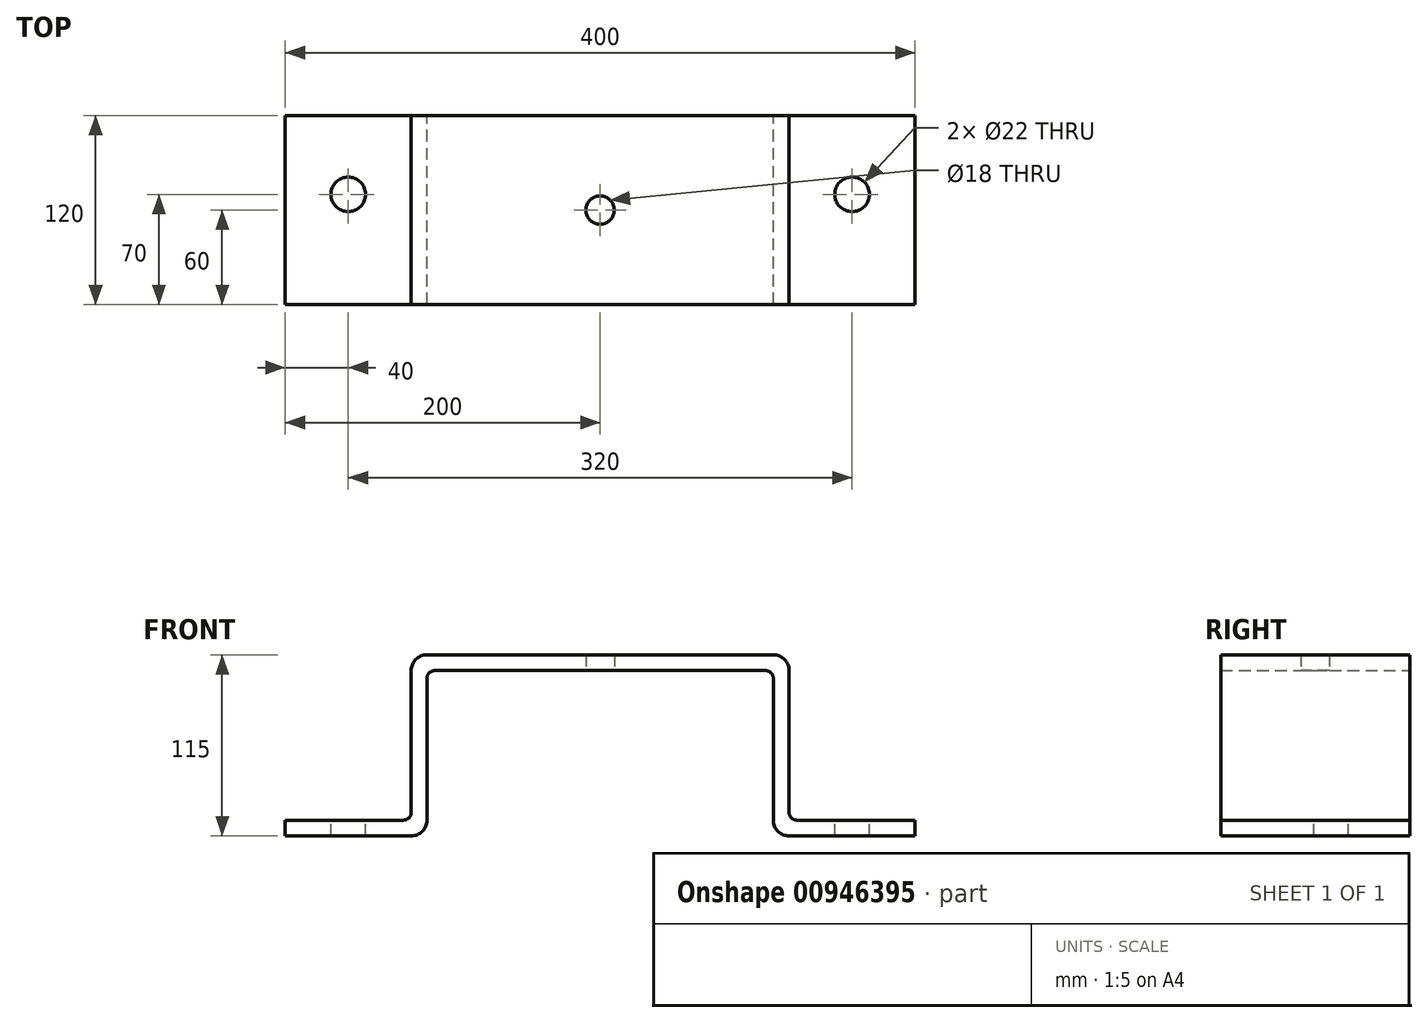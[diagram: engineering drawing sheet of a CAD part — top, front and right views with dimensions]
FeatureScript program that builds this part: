
annotation { "Feature Type Name" : "Feature", "Feature Type Description" : "" }
export const myFeature = defineFeature(function(context is Context, id is Id, definition is map)
    precondition{}
    {
        {
            var Q0;
            Q0=qCreatedBy(makeId("Front.planeOp"),FACE);
            var sketch = newSketch(context, id + "F0", { "sketchPlane" : qUnion([Q0])});
            skLineSegment(sketch, "E0.bottom", {"start": v(-200, 0) * mm, "end": v(200, 0) * mm});
            skLineSegment(sketch, "E0.top", {"start": v(-200, 115) * mm, "end": v(200, 115) * mm});
            skLineSegment(sketch, "E0.left", {"start": v(-200, 0) * mm, "end": v(-200, 115) * mm});
            skLineSegment(sketch, "E0.right", {"start": v(200, 0) * mm, "end": v(200, 115) * mm});
            skPoint(sketch, "E1", {"position": v(0, 0) * mm});
            skLineSegment(sketch, "E2", {"start": v(0, 0) * mm, "end": v(0, 115) * mm, "construction": true});
            skPoint(sketch, "E3", {"position": v(0, 52.5) * mm});
            skLineSegment(sketch, "E4.bottom", {"start": v(110, 0) * mm, "end": v(-110, 0) * mm});
            skLineSegment(sketch, "E4.top", {"start": v(110, 105) * mm, "end": v(-110, 105) * mm});
            skLineSegment(sketch, "E4.left", {"start": v(110, 0) * mm, "end": v(110, 105) * mm});
            skLineSegment(sketch, "E4.right", {"start": v(-110, 0) * mm, "end": v(-110, 105) * mm});
            skLineSegment(sketch, "E5.0", {"start": v(-200, 10) * mm, "end": v(-120, 10) * mm});
            skLineSegment(sketch, "E6.trimOffspring", {"start": v(120, 10) * mm, "end": v(200, 10) * mm});
            skLineSegment(sketch, "E7.0", {"start": v(120, 10) * mm, "end": v(120, 115) * mm});
            skLineSegment(sketch, "E8.0", {"start": v(-120, 10) * mm, "end": v(-120, 115) * mm});
            skSolve(sketch);
        }
        {
            var Q0;
            Q0=makeQuery(id+"F0.imprint","IMPRINT",FACE,{"disambiguationData":[TD([[makeQuery(id+"F0.imprint","IMPRINT",EDGE,{"derivedFrom":sQuery(id+"F0.wireOp",EDGE,"E4.top")}),-1.0]])]});
            extrude(context, id + "F1", {"entities" : qUnion([Q0]), "depth" : 120 * mm, "offsetDistance" : 25 * mm});
        }
        {
            var Q0;
            Q0=makeQuery(id+"F1.opExtrude","SWEPT_FACE",FACE,{"disambiguationData":[OSD([sQuery(id+"F0.wireOp",EDGE,"E6.trimOffspring")])]});
            var sketch = newSketch(context, id + "F2", { "sketchPlane" : qUnion([Q0])});
            skLineSegment(sketch, "E9", {"start": v(160, 0) * mm, "end": v(160, -120) * mm, "construction": true});
            skPoint(sketch, "E10", {"position": v(160, -50) * mm});
            skLineSegment(sketch, "E11.MirrorCS", {"start": v(-160, 0) * mm, "end": v(-160, -120) * mm, "construction": true});
            skPoint(sketch, "E12.MirrorP", {"position": v(-160, -50) * mm});
            skLineSegment(sketch, "E13", {"start": v(0, 0) * mm, "end": v(0, -120) * mm, "construction": true});
            skPoint(sketch, "E14", {"position": v(0, -60) * mm});
            skSolve(sketch);
        }
        {
            var Q0;
            Q0=sQuery(id+"F2.wireOp",VERTEX,"E10");
            var Q1;
            Q1=sQuery(id+"F2.wireOp",VERTEX,"E12.MirrorP");
            var Q2;
            Q2=makeQuery(id+"F1.opExtrude","SWEPT_BODY",BODY,{"disambiguationData":[OSD([sQuery(id+"F0.wireOp",EDGE,"E0.bottom"),sQuery(id+"F0.wireOp",EDGE,"E0.top"),sQuery(id+"F0.wireOp",EDGE,"E0.left"),sQuery(id+"F0.wireOp",EDGE,"E0.right"),sQuery(id+"F0.wireOp",EDGE,"E4.top"),sQuery(id+"F0.wireOp",EDGE,"E4.left"),sQuery(id+"F0.wireOp",EDGE,"E4.right"),sQuery(id+"F0.wireOp",EDGE,"E5.0"),sQuery(id+"F0.wireOp",EDGE,"E6.trimOffspring"),sQuery(id+"F0.wireOp",EDGE,"E7.0"),sQuery(id+"F0.wireOp",EDGE,"E8.0")])]});
            hole(context, id + "F3", {"style" : HoleStyle.SIMPLE, "endStyle" : HoleEndStyle.THROUGH, "holeDiameter" : 22 * mm, "majorDiameter" : 5 * mm, "tappedDepth" : 12 * mm, "tapClearance" : 3, "locations" : qUnion([Q0, Q1]), "scope" : qUnion([Q2])});
        }
        {
            var Q0;
            Q0=sQuery(id+"F2.wireOp",VERTEX,"E14");
            var Q1;
            Q1=makeQuery(id+"F1.opExtrude","SWEPT_BODY",BODY,{"disambiguationData":[OSD([sQuery(id+"F0.wireOp",EDGE,"E0.bottom"),sQuery(id+"F0.wireOp",EDGE,"E0.top"),sQuery(id+"F0.wireOp",EDGE,"E0.left"),sQuery(id+"F0.wireOp",EDGE,"E0.right"),sQuery(id+"F0.wireOp",EDGE,"E4.top"),sQuery(id+"F0.wireOp",EDGE,"E4.left"),sQuery(id+"F0.wireOp",EDGE,"E4.right"),sQuery(id+"F0.wireOp",EDGE,"E5.0"),sQuery(id+"F0.wireOp",EDGE,"E6.trimOffspring"),sQuery(id+"F0.wireOp",EDGE,"E7.0"),sQuery(id+"F0.wireOp",EDGE,"E8.0")])]});
            hole(context, id + "F4", {"style" : HoleStyle.SIMPLE, "endStyle" : HoleEndStyle.THROUGH, "oppositeDirection" : true, "holeDiameter" : 18 * mm, "majorDiameter" : 5 * mm, "tappedDepth" : 12 * mm, "tapClearance" : 3, "locations" : qUnion([Q0]), "scope" : qUnion([Q1])});
        }
        {
            var Q0;
            Q0=makeQuery(id+"F1.opExtrude","SWEPT_EDGE",EDGE,{"disambiguationData":[OSD([sQuery(id+"F0.wireOp",EDGE,"E0.top"),sQuery(id+"F0.wireOp",EDGE,"E8.0")])]});
            var Q1;
            Q1=makeQuery(id+"F1.opExtrude","SWEPT_EDGE",EDGE,{"disambiguationData":[OSD([sQuery(id+"F0.wireOp",EDGE,"E0.top"),sQuery(id+"F0.wireOp",EDGE,"E7.0")])]});
            var Q2;
            Q2=makeQuery(id+"F1.opExtrude","SWEPT_EDGE",EDGE,{"disambiguationData":[OSD([sQuery(id+"F0.wireOp",EDGE,"E0.bottom"),sQuery(id+"F0.wireOp",EDGE,"E4.bottom"),sQuery(id+"F0.wireOp",EDGE,"E4.left")])]});
            var Q3;
            Q3=makeQuery(id+"F1.opExtrude","SWEPT_EDGE",EDGE,{"disambiguationData":[OSD([sQuery(id+"F0.wireOp",EDGE,"E0.bottom"),sQuery(id+"F0.wireOp",EDGE,"E4.bottom"),sQuery(id+"F0.wireOp",EDGE,"E4.right")])]});
            fillet(context, id + "F5", {"entities" : qUnion([Q0, Q1, Q2, Q3]), "radius" : 10 * mm, "tangentPropagation" : true, "allowEdgeOverflow" : false});
        }
        {
            var Q0;
            Q0=makeQuery(id+"F1.opExtrude","SWEPT_EDGE",EDGE,{"disambiguationData":[OSD([sQuery(id+"F0.wireOp",EDGE,"E4.top"),sQuery(id+"F0.wireOp",EDGE,"E4.right")])]});
            var Q1;
            Q1=makeQuery(id+"F1.opExtrude","SWEPT_EDGE",EDGE,{"disambiguationData":[OSD([sQuery(id+"F0.wireOp",EDGE,"E4.top"),sQuery(id+"F0.wireOp",EDGE,"E4.left")])]});
            var Q2;
            Q2=makeQuery(id+"F1.opExtrude","SWEPT_EDGE",EDGE,{"disambiguationData":[OSD([sQuery(id+"F0.wireOp",EDGE,"E6.trimOffspring"),sQuery(id+"F0.wireOp",EDGE,"E7.0")])]});
            var Q3;
            Q3=makeQuery(id+"F1.opExtrude","SWEPT_EDGE",EDGE,{"disambiguationData":[OSD([sQuery(id+"F0.wireOp",EDGE,"E5.0"),sQuery(id+"F0.wireOp",EDGE,"E8.0")])]});
            fillet(context, id + "F6", {"entities" : qUnion([Q0, Q1, Q2, Q3]), "radius" : 5 * mm, "tangentPropagation" : true, "allowEdgeOverflow" : false});
        }
    });
